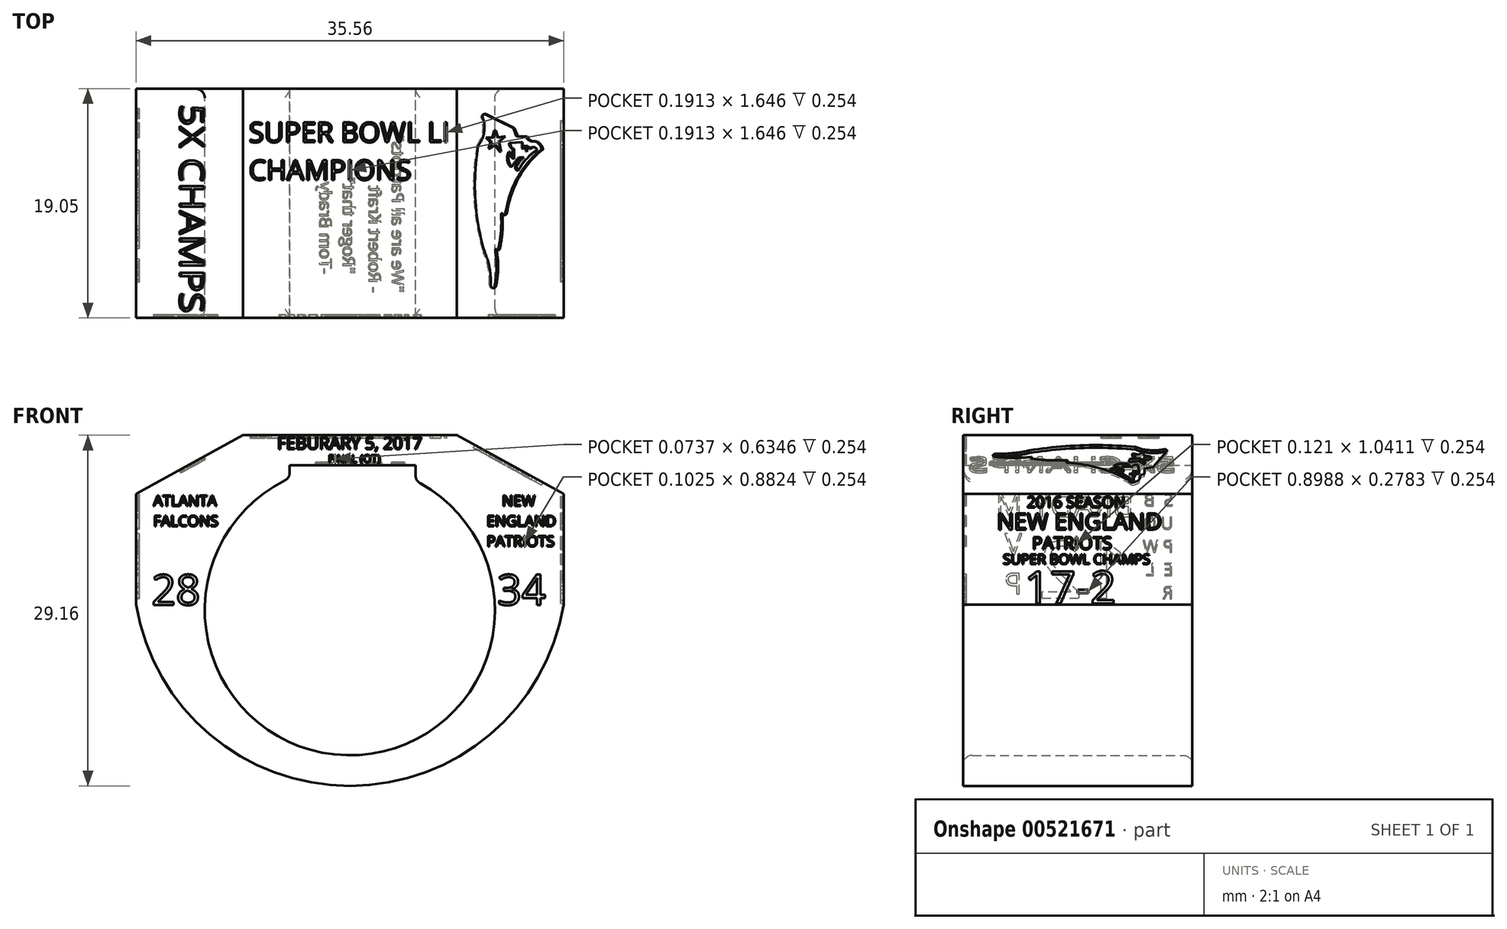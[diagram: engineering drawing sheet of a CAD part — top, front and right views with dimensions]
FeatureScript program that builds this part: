
annotation { "Feature Type Name" : "Feature", "Feature Type Description" : "" }
export const myFeature = defineFeature(function(context is Context, id is Id, definition is map)
    precondition{}
    {
        {
            var Q0;
            Q0=qCreatedBy(makeId("Front.planeOp"),FACE);
            var sketch = newSketch(context, id + "F0", { "sketchPlane" : qUnion([Q0])});
            skArc(sketch, "E0", {"start": v(-17.78, 0) * mm, "mid": v(0, -15.06) * mm, "end": v(17.78, 0) * mm});
            skLineSegment(sketch, "E1", {"start": v(-17.78, 0) * mm, "end": v(-17.78, 9.21) * mm});
            skLineSegment(sketch, "E2", {"start": v(17.78, 9.21) * mm, "end": v(17.78, 0) * mm});
            skCircle(sketch, "E3", {"center": v(0, -0.45) * mm, "radius": 12.07 * mm, "construction": true});
            skArc(sketch, "E4", {"start": v(-8.89, 14.1) * mm, "mid": v(-13.68, 12.28) * mm, "end": v(-17.78, 9.21) * mm, "construction": true});
            skArc(sketch, "E5", {"start": v(17.78, 9.21) * mm, "mid": v(13.68, 12.28) * mm, "end": v(8.89, 14.1) * mm, "construction": true});
            skLineSegment(sketch, "E6", {"start": v(-8.89, 14.1) * mm, "end": v(8.9, 14.1) * mm});
            skLineSegment(sketch, "E7", {"start": v(-12.07, -0.45) * mm, "end": v(-17.78, -0.45) * mm, "construction": true});
            skLineSegment(sketch, "E8", {"start": v(12.06, -0.45) * mm, "end": v(17.78, -0.45) * mm, "construction": true});
            skLineSegment(sketch, "E9", {"start": v(-8.9, 14.1) * mm, "end": v(-17.78, 9.21) * mm});
            skLineSegment(sketch, "E10", {"start": v(8.9, 14.1) * mm, "end": v(17.78, 9.21) * mm});
            skLineSegment(sketch, "E11", {"start": v(5.46, 11.61) * mm, "end": v(-5.01, 11.61) * mm});
            skArc(sketch, "E12", {"start": v(-5.01, 10.52) * mm, "mid": v(-0.25, -12.52) * mm, "end": v(5.46, 10.3) * mm});
            skLineSegment(sketch, "E13", {"start": v(5.46, 10.3) * mm, "end": v(5.46, 11.61) * mm});
            skLineSegment(sketch, "E14", {"start": v(-5.01, 10.52) * mm, "end": v(-5.01, 11.61) * mm});
            skSolve(sketch);
        }
        {
            var Q0;
            Q0 = qSketchRegion(id + "F0", true);
            extrude(context, id + "F1", {"entities" : qUnion([Q0]), "depth" : 19.05 * mm, "offsetDistance" : 25.4 * mm});
        }
        {
            var Q0;
            Q0=makeQuery(id+"F1.opExtrude","SWEPT_FACE",FACE,{"disambiguationData":[OSD([sQuery(id+"F0.wireOp",EDGE,"E2")])]});
            var sketch = newSketch(context, id + "F2", { "sketchPlane" : qUnion([Q0])});
            skText(sketch, "E15", { "text": "NEW ENGLAND ", "fontName": "OpenSans-Regular.ttf"});
            skText(sketch, "E16", { "text": "PATRIOTS", "fontName": "OpenSans-Regular.ttf"});
            skText(sketch, "E17", { "text": "17-2", "fontName": "OpenSans-Regular.ttf"});
            skText(sketch, "E18", { "text": "SUPER BOWL CHAMPS", "fontName": "OpenSans-Regular.ttf"});
            skText(sketch, "E19", { "text": "2016 SEASON", "fontName": "OpenSans-Regular.ttf"});
            const initialGuessF2  = {"E15": [-0.01626, 0.00624, 1, 0, 0.00138], "E16": [-0.01334, 0.0046, 1, 0, 0.00105], "E17": [-0.01398, 0.00011, 1, 0, 0.0027], "E18": [-0.01575, 0.00337, 1, 0, 0.00084], "E19": [-0.01377, 0.00807, 1, 0, 0.00093]};
            skSetInitialGuess(sketch, initialGuessF2);
            skSolve(sketch);
        }
        {
            var Q0;
            Q0 = qSketchRegion(id + "F2", true);
            extrude(context, id + "F3", {"entities" : qUnion([Q0]), "operationType" : NewBodyOperationType.REMOVE, "oppositeDirection" : true, "depth" : 0.25 * mm, "offsetDistance" : 25.4 * mm});
        }
        {
            var Q0;
            Q0=makeQuery(id+"F1.opExtrude","SWEPT_FACE",FACE,{"disambiguationData":[OSD([sQuery(id+"F0.wireOp",EDGE,"E1")])]});
            var sketch = newSketch(context, id + "F4", { "sketchPlane" : qUnion([Q0])});
            skLineSegment(sketch, "E20.bottom", {"start": v(4.85, 9.21) * mm, "end": v(13.5, 9.21) * mm, "construction": true});
            skLineSegment(sketch, "E20.top", {"start": v(4.85, 7.3) * mm, "end": v(13.5, 7.3) * mm, "construction": true});
            skLineSegment(sketch, "E20.left", {"start": v(4.85, 9.21) * mm, "end": v(4.85, 7.3) * mm, "construction": true});
            skLineSegment(sketch, "E20.right", {"start": v(13.5, 9.21) * mm, "end": v(13.5, 7.3) * mm, "construction": true});
            skText(sketch, "E21", { "text": "BRADY", "fontName": "OpenSans-Regular.ttf"});
            skText(sketch, "E22", { "text": "12", "fontName": "OpenSans-Regular.ttf"});
            skText(sketch, "E23", { "text": "S  B\nU O\nP W\nE  L\nR", "fontName": "OpenSans-Regular.ttf"});
            skText(sketch, "E24", { "text": "M\nV\nP", "fontName": "OpenSans-Regular.ttf"});
            const initialGuessF4  = {"E21": [0.00485, 0.0073, 1, 0, 0.00191], "E22": [0.00533, 0.00055, 1, 0, 0.00474], "E23": [0.00159, 0.0082, 1, 0, 0.00102], "E24": [0.01416, 0.00747, 1, 0, 0.00174]};
            skSetInitialGuess(sketch, initialGuessF4);
            skSolve(sketch);
        }
        {
            var Q0;
            Q0 = qSketchRegion(id + "F4", true);
            extrude(context, id + "F5", {"entities" : qUnion([Q0]), "operationType" : NewBodyOperationType.REMOVE, "oppositeDirection" : true, "depth" : 0.25 * mm, "offsetDistance" : 25.4 * mm});
        }
        {
            var Q0;
            Q0=makeQuery(id+"F1.opExtrude","CAP_FACE",FACE,{"disambiguationData":[OSD([sQuery(id+"F0.wireOp",EDGE,"E0"),sQuery(id+"F0.wireOp",EDGE,"E1"),sQuery(id+"F0.wireOp",EDGE,"E2"),sQuery(id+"F0.wireOp",EDGE,"E3"),sQuery(id+"F0.wireOp",EDGE,"E4"),sQuery(id+"F0.wireOp",EDGE,"E5"),sQuery(id+"F0.wireOp",EDGE,"E6")])],"isStart":false});
            var sketch = newSketch(context, id + "F6", { "sketchPlane" : qUnion([Q0])});
            skText(sketch, "E25", { "text": "FEBURARY 5, 2017", "fontName": "OpenSans-Regular.ttf"});
            skText(sketch, "E26", { "text": "ATLANTA \nFALCONS", "fontName": "OpenSans-Regular.ttf"});
            skText(sketch, "E27", { "text": "28", "fontName": "OpenSans-Regular.ttf"});
            skLineSegment(sketch, "E28", {"start": v(-10.92, 9.1) * mm, "end": v(11.37, 9.1) * mm, "construction": true});
            skText(sketch, "E29", { "text": "    NEW\nENGLAND\nPATRIOTS", "fontName": "OpenSans-Regular.ttf"});
            skText(sketch, "E30", { "text": "34\n", "fontName": "OpenSans-Regular.ttf"});
            skLineSegment(sketch, "E31", {"start": v(-12.4, 2.52) * mm, "end": v(12.25, 2.52) * mm, "construction": true});
            skText(sketch, "E32", { "text": "FINAL (OT)", "fontName": "OpenSans-Regular.ttf"});
            const initialGuessF6  = {"E25": [-0.00603, 0.01293, 1, 0, 0.00102], "E26": [-0.01635, 0.0082, 1, 0, 0.00089], "E27": [-0.01648, -2e-05, 1, 0, 0.00254], "E29": [0.01137, 0.0082, 1, 0, 0.00089], "E30": [0.01225, -2e-05, 1, 0, 0.00254], "E32": [-0.0018, 0.01183, 1, 0, 0.00064]};
            skSetInitialGuess(sketch, initialGuessF6);
            skSolve(sketch);
        }
        {
            var Q0;
            Q0 = qSketchRegion(id + "F6", true);
            extrude(context, id + "F7", {"entities" : qUnion([Q0]), "operationType" : NewBodyOperationType.REMOVE, "oppositeDirection" : true, "depth" : 0.25 * mm, "offsetDistance" : 25.4 * mm});
        }
        {
            var Q0;
            Q0=makeQuery(id+"F1.opExtrude","CAP_EDGE",EDGE,{"disambiguationData":[OSD([sQuery(id+"F0.wireOp",EDGE,"E12")])],"isStart":false});
            var Q1;
            Q1=makeQuery(id+"F1.opExtrude","CAP_EDGE",EDGE,{"disambiguationData":[OSD([sQuery(id+"F0.wireOp",EDGE,"E12")])],"isStart":true});
            var Q2;
            Q2=makeQuery(id+"F1.opExtrude","SWEPT_EDGE",EDGE,{"disambiguationData":[OSD([sQuery(id+"F0.wireOp",EDGE,"E12"),sQuery(id+"F0.wireOp",EDGE,"E13")])]});
            var Q3;
            Q3=makeQuery(id+"F1.opExtrude","SWEPT_EDGE",EDGE,{"disambiguationData":[OSD([sQuery(id+"F0.wireOp",EDGE,"E12"),sQuery(id+"F0.wireOp",EDGE,"E14")])]});
            fillet(context, id + "F8", {"entities" : qUnion([Q0, Q1, Q2, Q3]), "radius" : 0.76 * mm, "tangentPropagation" : true, "allowEdgeOverflow" : false});
        }
        {
            var Q0;
            Q0=makeQuery(id+"F1.opExtrude","SWEPT_FACE",FACE,{"disambiguationData":[OSD([sQuery(id+"F0.wireOp",EDGE,"E6")])]});
            var sketch = newSketch(context, id + "F9", { "sketchPlane" : qUnion([Q0])});
            skText(sketch, "E33", { "text": "SUPER BOWL LI \nCHAMPIONS", "fontName": "OpenSans-Regular.ttf"});
            const initialGuessF9  = {"E33": [-0.00841, -0.00445, 1, 0, 0.00166]};
            skSetInitialGuess(sketch, initialGuessF9);
            skSolve(sketch);
        }
        {
            var Q0;
            Q0 = qSketchRegion(id + "F9", true);
            extrude(context, id + "F10", {"entities" : qUnion([Q0]), "operationType" : NewBodyOperationType.REMOVE, "oppositeDirection" : true, "depth" : 0.25 * mm, "offsetDistance" : 25.4 * mm});
        }
        {
            var Q0;
            Q0=makeQuery(id+"F1.opExtrude","SWEPT_FACE",FACE,{"disambiguationData":[OSD([sQuery(id+"F0.wireOp",EDGE,"E10")])]});
            var sketch = newSketch(context, id + "F11", { "sketchPlane" : qUnion([Q0])});
            skArc(sketch, "E34", {"start": v(4.21, -16.3) * mm, "mid": v(4.45, -16.58) * mm, "end": v(4.73, -16.35) * mm});
            skArc(sketch, "E35", {"start": v(4.21, -16.3) * mm, "mid": v(4.1, -14.9) * mm, "end": v(3.63, -13.57) * mm});
            skArc(sketch, "E36", {"start": v(3.04, -4.71) * mm, "mid": v(2.74, -9.18) * mm, "end": v(3.63, -13.57) * mm});
            skArc(sketch, "E37", {"start": v(3.04, -4.71) * mm, "mid": v(3.6, -3.57) * mm, "end": v(3.42, -2.32) * mm});
            skArc(sketch, "E38", {"start": v(3.82, -2.14) * mm, "mid": v(3.57, -2.12) * mm, "end": v(3.42, -2.32) * mm});
            skLineSegment(sketch, "E39", {"start": v(3.82, -2.14) * mm, "end": v(6.48, -3.28) * mm});
            skLineSegment(sketch, "E40", {"start": v(6.48, -3.28) * mm, "end": v(6.8, -3.96) * mm});
            skLineSegment(sketch, "E41", {"start": v(6.8, -3.96) * mm, "end": v(7.67, -3.96) * mm});
            skLineSegment(sketch, "E42", {"start": v(7.67, -3.96) * mm, "end": v(7.83, -4.23) * mm});
            skLineSegment(sketch, "E43", {"start": v(7.83, -4.23) * mm, "end": v(8.19, -4.38) * mm});
            skArc(sketch, "E44", {"start": v(9.17, -5.05) * mm, "mid": v(8.82, -4.5) * mm, "end": v(8.19, -4.38) * mm});
            skArc(sketch, "E45", {"start": v(9.17, -5.05) * mm, "mid": v(6.91, -7.34) * mm, "end": v(5.75, -10.35) * mm});
            skArc(sketch, "E46", {"start": v(5.32, -10.35) * mm, "mid": v(5.54, -10.5) * mm, "end": v(5.75, -10.35) * mm});
            skArc(sketch, "E47", {"start": v(5.08, -13.25) * mm, "mid": v(5.33, -11.8) * mm, "end": v(5.32, -10.35) * mm});
            skArc(sketch, "E48", {"start": v(4.75, -13.34) * mm, "mid": v(4.95, -13.43) * mm, "end": v(5.08, -13.25) * mm});
            skArc(sketch, "E49", {"start": v(4.73, -16.35) * mm, "mid": v(4.91, -14.85) * mm, "end": v(4.75, -13.34) * mm});
            skLineSegment(sketch, "E50", {"start": v(4.34, -4.45) * mm, "end": v(3.9, -4.05) * mm});
            skLineSegment(sketch, "E51", {"start": v(3.9, -4.05) * mm, "end": v(4.48, -4.05) * mm});
            skLineSegment(sketch, "E52", {"start": v(4.48, -4.05) * mm, "end": v(4.7, -3.45) * mm});
            skLineSegment(sketch, "E53", {"start": v(4.7, -3.45) * mm, "end": v(4.9, -4.05) * mm});
            skLineSegment(sketch, "E54", {"start": v(4.9, -4.05) * mm, "end": v(5.59, -3.95) * mm});
            skLineSegment(sketch, "E55", {"start": v(5.59, -3.95) * mm, "end": v(5, -4.4) * mm});
            skLineSegment(sketch, "E56", {"start": v(5, -4.4) * mm, "end": v(5.2, -5.24) * mm});
            skLineSegment(sketch, "E57", {"start": v(5.2, -5.24) * mm, "end": v(4.7, -4.68) * mm});
            skLineSegment(sketch, "E58", {"start": v(4.7, -4.68) * mm, "end": v(4.15, -4.98) * mm});
            skLineSegment(sketch, "E59", {"start": v(4.15, -4.98) * mm, "end": v(4.34, -4.45) * mm});
            skLineSegment(sketch, "E60", {"start": v(6.44, -5.83) * mm, "end": v(6.44, -5) * mm});
            skArc(sketch, "E61", {"start": v(6.06, -5.25) * mm, "mid": v(6.14, -5.6) * mm, "end": v(6.44, -5.83) * mm});
            skArc(sketch, "E62", {"start": v(6.1, -4.52) * mm, "mid": v(6.17, -4.83) * mm, "end": v(6.44, -5) * mm});
            skLineSegment(sketch, "E63", {"start": v(6.1, -4.52) * mm, "end": v(7.21, -4.43) * mm});
            skLineSegment(sketch, "E64", {"start": v(7.21, -4.43) * mm, "end": v(7.21, -4.91) * mm});
            skLineSegment(sketch, "E65", {"start": v(7.21, -4.91) * mm, "end": v(7.29, -5) * mm});
            skArc(sketch, "E66", {"start": v(7.29, -5) * mm, "mid": v(7.36, -4.89) * mm, "end": v(7.4, -4.76) * mm});
            skLineSegment(sketch, "E67", {"start": v(7.4, -4.76) * mm, "end": v(7.54, -4.76) * mm});
            skLineSegment(sketch, "E68", {"start": v(7.54, -4.76) * mm, "end": v(7.54, -5) * mm});
            skLineSegment(sketch, "E69", {"start": v(7.54, -5) * mm, "end": v(7.67, -5.24) * mm});
            skLineSegment(sketch, "E70", {"start": v(7.67, -5.24) * mm, "end": v(7.67, -4.76) * mm});
            skLineSegment(sketch, "E71", {"start": v(7.67, -4.76) * mm, "end": v(7.9, -4.88) * mm});
            skLineSegment(sketch, "E72", {"start": v(7.9, -4.88) * mm, "end": v(7.9, -5) * mm});
            skLineSegment(sketch, "E73", {"start": v(7.9, -5) * mm, "end": v(8.21, -4.88) * mm});
            skArc(sketch, "E74", {"start": v(8.6, -5.12) * mm, "mid": v(8.47, -4.9) * mm, "end": v(8.21, -4.88) * mm});
            skArc(sketch, "E75", {"start": v(8.6, -5.12) * mm, "mid": v(7.6, -5.84) * mm, "end": v(6.83, -6.8) * mm});
            skArc(sketch, "E76", {"start": v(6.83, -6.28) * mm, "mid": v(6.66, -6.54) * mm, "end": v(6.83, -6.8) * mm});
            skArc(sketch, "E77", {"start": v(7.38, -5.72) * mm, "mid": v(7.05, -5.95) * mm, "end": v(6.83, -6.28) * mm});
            skLineSegment(sketch, "E78", {"start": v(7.38, -5.72) * mm, "end": v(6.9, -5.72) * mm});
            skLineSegment(sketch, "E79", {"start": v(6.9, -5.72) * mm, "end": v(6.22, -6.48) * mm});
            skArc(sketch, "E80", {"start": v(6.06, -5.25) * mm, "mid": v(5.9, -5.9) * mm, "end": v(6.22, -6.48) * mm});
            skSolve(sketch);
        }
        {
            var Q0;
            Q0 = qSketchRegion(id + "F11", true);
            extrude(context, id + "F12", {"entities" : qUnion([Q0]), "operationType" : NewBodyOperationType.REMOVE, "oppositeDirection" : true, "depth" : 0.25 * mm, "offsetDistance" : 25.4 * mm});
        }
        {
            var Q0;
            Q0=makeQuery(id+"F1.opExtrude","SWEPT_FACE",FACE,{"disambiguationData":[OSD([sQuery(id+"F0.wireOp",EDGE,"E9")])]});
            var sketch = newSketch(context, id + "F13", { "sketchPlane" : qUnion([Q0])});
            skText(sketch, "E81", { "text": "5X CHAMPS", "fontName": "OpenSans-Regular.ttf"});
            const initialGuessF13  = {"E81": [-0.007, -0.00128, 0, -1, 0.00229]};
            skSetInitialGuess(sketch, initialGuessF13);
            skSolve(sketch);
        }
        {
            var Q0;
            Q0 = qSketchRegion(id + "F13", true);
            extrude(context, id + "F14", {"entities" : qUnion([Q0]), "operationType" : NewBodyOperationType.REMOVE, "oppositeDirection" : true, "depth" : 0.25 * mm, "offsetDistance" : 25.4 * mm});
        }
        {
            var Q0;
            Q0=makeQuery(id+"F1.opExtrude","SWEPT_FACE",FACE,{"disambiguationData":[OSD([sQuery(id+"F0.wireOp",EDGE,"E11")])]});
            var sketch = newSketch(context, id + "F15", { "sketchPlane" : qUnion([Q0])});
            skText(sketch, "E82", { "text": "\"We are all Patriots\"\n- Robert Kraft", "fontName": "OpenSans-Regular.ttf"});
            skText(sketch, "E83", { "text": "\"Roger that\"\n-Tom Brady", "fontName": "OpenSans-Regular.ttf"});
            const initialGuessF15  = {"E82": [0.00348, 0.01695, 0, -1, 0.00102], "E83": [-0.0006, 0.01539, 0, -1, 0.00102]};
            skSetInitialGuess(sketch, initialGuessF15);
            skSolve(sketch);
        }
        {
            var Q0;
            Q0 = qSketchRegion(id + "F15", true);
            extrude(context, id + "F16", {"entities" : qUnion([Q0]), "operationType" : NewBodyOperationType.REMOVE, "oppositeDirection" : true, "depth" : 0.25 * mm, "offsetDistance" : 25.4 * mm});
        }
    });
